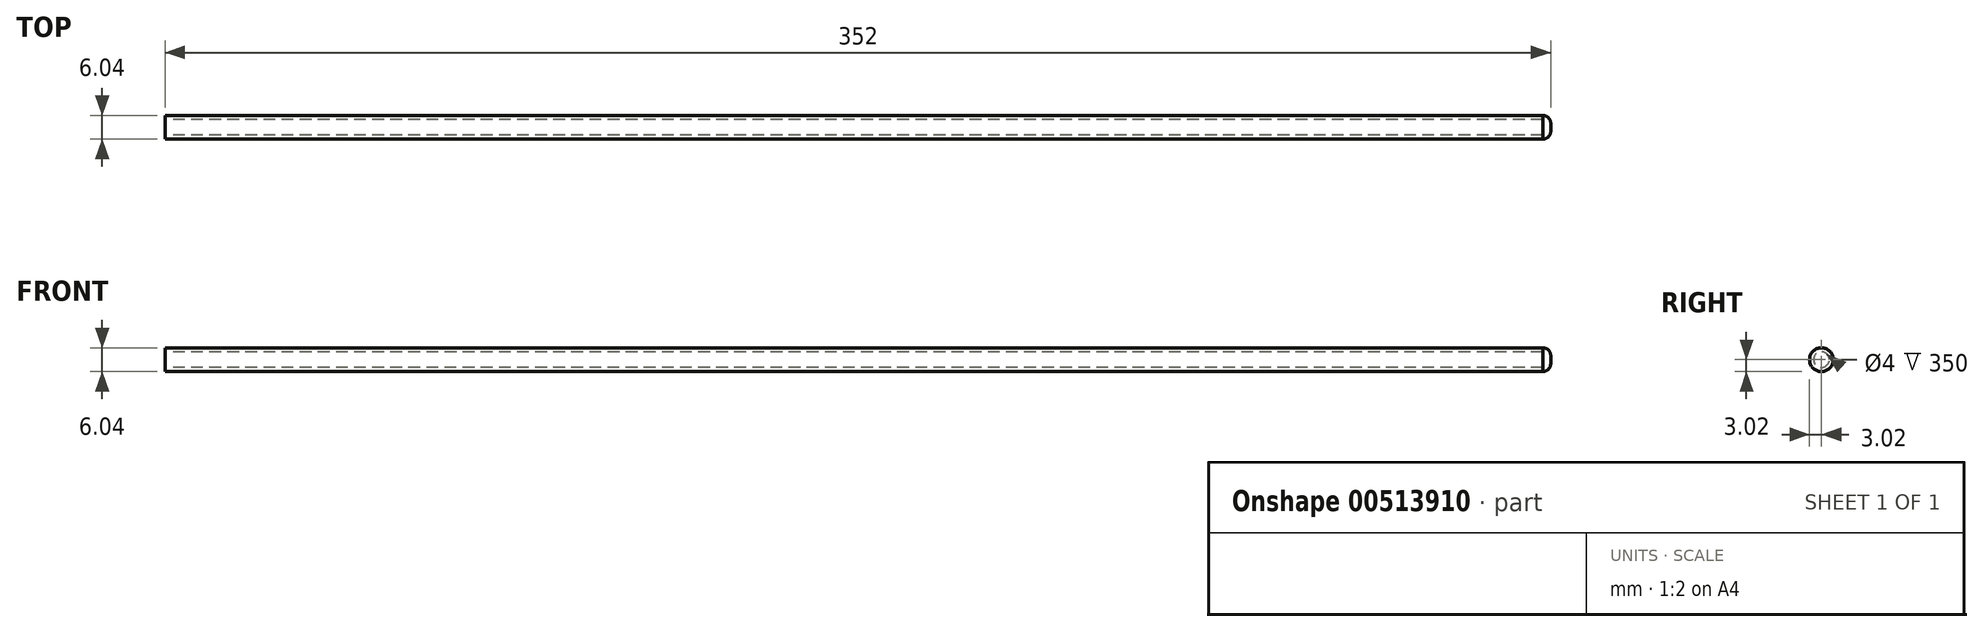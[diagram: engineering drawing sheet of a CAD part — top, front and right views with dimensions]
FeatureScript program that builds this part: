
annotation { "Feature Type Name" : "Feature", "Feature Type Description" : "" }
export const myFeature = defineFeature(function(context is Context, id is Id, definition is map)
    precondition{}
    {
        {
            var Q0;
            Q0=qCreatedBy(makeId("Right.planeOp"),FACE);
            var sketch = newSketch(context, id + "F0", { "sketchPlane" : qUnion([Q0])});
            skCircle(sketch, "E0", {"center": v(0, 0) * mm, "radius": 2 * mm});
            skCircle(sketch, "E1", {"center": v(0, 0) * mm, "radius": 3 * mm});
            skSolve(sketch);
        }
        {
            var Q0;
            Q0=makeQuery(id+"F0.imprint","IMPRINT",FACE,{"disambiguationData":[TD([[makeQuery(id+"F0.imprint","IMPRINT",EDGE,{"derivedFrom":sQuery(id+"F0.wireOp",EDGE,"E0")}),-1.0]])]});
            extrude(context, id + "F1", {"entities" : qUnion([Q0]), "depth" : 350 * mm});
        }
        {
            var Q0;
            Q0=makeQuery(id+"F1.opExtrude","CAP_FACE",FACE,{"disambiguationData":[OSD([sQuery(id+"F0.wireOp",EDGE,"E0"),sQuery(id+"F0.wireOp",EDGE,"E1")])],"isStart":false});
            var sketch = newSketch(context, id + "F2", { "sketchPlane" : qUnion([Q0])});
            skCircle(sketch, "E2", {"center": v(0, 0) * mm, "radius": 3.02 * mm});
            skSolve(sketch);
        }
        {
            var Q0;
            Q0 = qSketchRegion(id + "F2", true);
            extrude(context, id + "F3", {"entities" : qUnion([Q0]), "operationType" : NewBodyOperationType.ADD, "depth" : 2 * mm});
        }
        {
            var Q0;
            Q0=makeQuery(id+"F3.opExtrude","CAP_EDGE",EDGE,{"disambiguationData":[OSD([sQuery(id+"F2.wireOp",EDGE,"E2")])],"isStart":false});
            fillet(context, id + "F4", {"entities" : qUnion([Q0]), "radius" : 2 * mm, "tangentPropagation" : true, "allowEdgeOverflow" : false});
        }
    });
